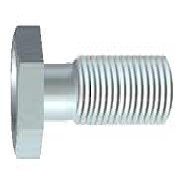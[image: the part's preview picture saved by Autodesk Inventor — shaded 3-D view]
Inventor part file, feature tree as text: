
AUTODESK INVENTOR PART (.ipt)
format: ipt  version: 2017.1 (Build 211199000, 199)  size: 178,176 bytes
history: native  units: mm (DEFAULTED — no unit token found)
features: sketch x4, extrude x2, chamfer x1, plane x1
ambient origin geometry x7: Origin, YZ Plane, XZ Plane, X Axis, Y Axis, Z Axis, Center Point
bodies: Solid1 (feature_tree), Body (feature_tree)
feature tree (8):
  extrude  "Head"  TaperAngle=90.0deg  [1 undecoded]
  extrude  "Indent"  TaperAngle=0.0deg  [1 undecoded]
  chamfer  "Chamfer1"  Distance=0.39751mm
  plane  "Work Plane1"
  sketch  "Sketch1"  dims[d1=4.1656mm d12=90.0deg]
  sketch  "Sketch2"  dims[d2=2.794mm d3=0.0mm]
  sketch  "Sketch4"  dims[d21=90.0deg d5=0.39751mm d6=0.39761mm d7=0.0mm d8=7.9248mm d9=26.9875mm d10=0.0mm d13=31.75mm d17=7.9248mm d18=6.33984mm d19=0.2804mm d20=0.0mm d77=45.0deg d80=0.0mm d81=0.0mm]
  sketch  "Sketch3"  dims[d4=30.0deg]
note: 2 required parameter values undecoded (feature->parameter linkage not recoverable at this tier; creation-order binding heuristic only, values carry confidence <= 0.55)
